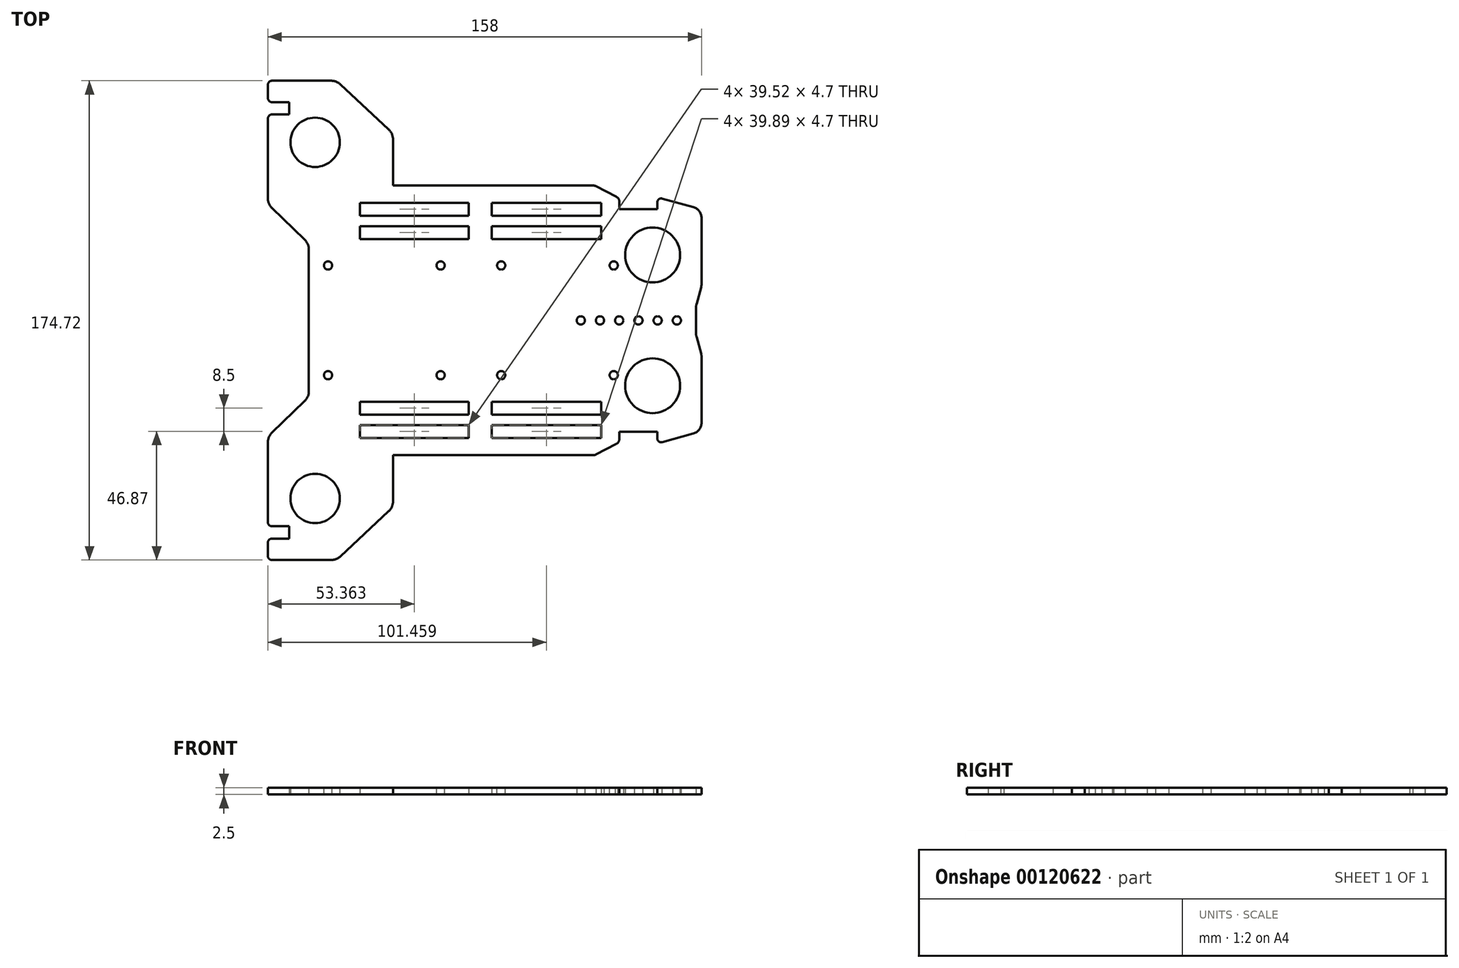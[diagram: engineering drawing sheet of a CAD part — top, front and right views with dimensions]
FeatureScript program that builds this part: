
annotation { "Feature Type Name" : "Feature", "Feature Type Description" : "" }
export const myFeature = defineFeature(function(context is Context, id is Id, definition is map)
    precondition{}
    {
        {
            var Q0;
            Q0=qCreatedBy(makeId("Top.planeOp"),FACE);
            var sketch = newSketch(context, id + "F0", { "sketchPlane" : qUnion([Q0])});
            skLineSegment(sketch, "E0", {"start": v(-81.12, -38.25) * mm, "end": v(74.88, -38.25) * mm});
            skLineSegment(sketch, "E1.bottom", {"start": v(-81.12, -117.81) * mm, "end": v(-73.32, -117.81) * mm});
            skLineSegment(sketch, "E1.top", {"start": v(-81.12, -113.31) * mm, "end": v(-73.32, -113.31) * mm});
            skLineSegment(sketch, "E1.right", {"start": v(-73.32, -117.81) * mm, "end": v(-73.32, -113.31) * mm});
            skLineSegment(sketch, "E2", {"start": v(-66.2, -38.25) * mm, "end": v(-66.2, -66.25) * mm});
            skLineSegment(sketch, "E3", {"start": v(-81.12, -80.61) * mm, "end": v(-66.2, -66.25) * mm});
            skLineSegment(sketch, "E4", {"start": v(-81.12, -80.61) * mm, "end": v(-81.12, -113.31) * mm});
            skLineSegment(sketch, "E5", {"start": v(-81.12, -125.61) * mm, "end": v(-56.12, -125.61) * mm});
            skLineSegment(sketch, "E6", {"start": v(-56.12, -125.61) * mm, "end": v(-35.53, -106.39) * mm});
            skLineSegment(sketch, "E7", {"start": v(-35.53, -106.39) * mm, "end": v(-35.53, -87.39) * mm});
            skLineSegment(sketch, "E8", {"start": v(-35.53, -87.39) * mm, "end": v(38, -87.39) * mm});
            skLineSegment(sketch, "E9", {"start": v(38, -87.39) * mm, "end": v(46.91, -82.75) * mm});
            skLineSegment(sketch, "E10", {"start": v(46.91, -82.75) * mm, "end": v(46.91, -78.85) * mm});
            skLineSegment(sketch, "E11", {"start": v(46.91, -78.85) * mm, "end": v(60.76, -78.85) * mm});
            skLineSegment(sketch, "E12", {"start": v(60.76, -78.85) * mm, "end": v(60.76, -83.16) * mm});
            skLineSegment(sketch, "E13", {"start": v(60.76, -83.16) * mm, "end": v(76.88, -78.68) * mm});
            skLineSegment(sketch, "E14", {"start": v(76.88, -78.68) * mm, "end": v(76.88, -51.04) * mm});
            skLineSegment(sketch, "E15", {"start": v(76.88, -51.04) * mm, "end": v(74.88, -43.67) * mm});
            skLineSegment(sketch, "E16", {"start": v(74.88, -43.67) * mm, "end": v(74.88, -38.25) * mm});
            skLineSegment(sketch, "E17", {"start": v(-81.12, -117.81) * mm, "end": v(-81.12, -125.61) * mm});
            skPoint(sketch, "E18.orphan", {"position": v(76.88, -38.25) * mm});
            skCircle(sketch, "E19", {"center": v(32.88, -38.25) * mm, "radius": 1.5 * mm});
            skCircle(sketch, "E20.1.0.0", {"center": v(39.88, -38.25) * mm, "radius": 1.5 * mm});
            skCircle(sketch, "E20.2.0.0", {"center": v(46.88, -38.25) * mm, "radius": 1.5 * mm});
            skCircle(sketch, "E20.3.0.0", {"center": v(53.88, -38.25) * mm, "radius": 1.5 * mm});
            skCircle(sketch, "E20.4.0.0", {"center": v(60.88, -38.25) * mm, "radius": 1.5 * mm});
            skCircle(sketch, "E20.5.0.0", {"center": v(67.88, -38.25) * mm, "radius": 1.5 * mm});
            skLineSegment(sketch, "E20.direction1", {"start": v(32.88, -38.25) * mm, "end": v(39.88, -38.25) * mm, "construction": true});
            skLineSegment(sketch, "E21.bottom", {"start": v(-47.51, -67.89) * mm, "end": v(-8, -67.89) * mm});
            skLineSegment(sketch, "E21.top", {"start": v(-47.51, -72.59) * mm, "end": v(-8, -72.59) * mm});
            skLineSegment(sketch, "E21.left", {"start": v(-47.51, -67.89) * mm, "end": v(-47.51, -72.59) * mm});
            skLineSegment(sketch, "E21.right", {"start": v(40.28, -67.89) * mm, "end": v(40.28, -72.59) * mm});
            skLineSegment(sketch, "E22.bottom", {"start": v(-47.51, -76.39) * mm, "end": v(-8, -76.39) * mm});
            skLineSegment(sketch, "E22.top", {"start": v(-47.51, -81.09) * mm, "end": v(-8, -81.09) * mm});
            skLineSegment(sketch, "E22.left", {"start": v(-47.51, -76.39) * mm, "end": v(-47.51, -81.09) * mm});
            skLineSegment(sketch, "E22.right", {"start": v(40.28, -76.39) * mm, "end": v(40.28, -81.09) * mm});
            skLineSegment(sketch, "E23", {"start": v(-8, -67.89) * mm, "end": v(-8, -72.59) * mm});
            skLineSegment(sketch, "E24", {"start": v(0.4, -67.89) * mm, "end": v(0.4, -72.59) * mm});
            skLineSegment(sketch, "E25.trimOffspring", {"start": v(0.4, -67.89) * mm, "end": v(40.28, -67.89) * mm});
            skLineSegment(sketch, "E26.trimOffspring", {"start": v(0.4, -72.59) * mm, "end": v(40.28, -72.59) * mm});
            skLineSegment(sketch, "E27.trimOffspring", {"start": v(0.4, -76.39) * mm, "end": v(40.28, -76.39) * mm});
            skLineSegment(sketch, "E28.trimOffspring", {"start": v(0.4, -81.09) * mm, "end": v(40.28, -81.09) * mm});
            skLineSegment(sketch, "E29.trimOffspring", {"start": v(-8, -76.39) * mm, "end": v(-8, -81.09) * mm});
            skLineSegment(sketch, "E30.trimOffspring", {"start": v(0.4, -76.39) * mm, "end": v(0.4, -81.09) * mm});
            skCircle(sketch, "E31", {"center": v(-63.9, -103.18) * mm, "radius": 9 * mm});
            skCircle(sketch, "E32", {"center": v(59.04, -62.08) * mm, "radius": 10 * mm});
            skSolve(sketch);
        }
        {
            var Q0;
            Q0=makeQuery(id+"F0.imprint","IMPRINT",FACE,{"disambiguationData":[TD([[makeQuery(id+"F0.imprint","IMPRINT",EDGE,{"derivedFrom":sQuery(id+"F0.wireOp",EDGE,"E1.bottom")}),-1.0]])]});
            extrude(context, id + "F1", {"entities" : qUnion([Q0]), "depth" : 2.5 * mm});
        }
        {
            var Q0;
            Q0=makeQuery(id+"F1.opExtrude","SWEPT_EDGE",EDGE,{"disambiguationData":[OSD([sQuery(id+"F0.wireOp",EDGE,"E12"),sQuery(id+"F0.wireOp",EDGE,"E13")])]});
            fillet(context, id + "F2", {"entities" : qUnion([Q0]), "radius" : 1.42 * mm, "tangentPropagation" : true, "allowEdgeOverflow" : false});
        }
        {
            var Q0;
            Q0=makeQuery(id+"F1.opExtrude","SWEPT_EDGE",EDGE,{"disambiguationData":[OSD([sQuery(id+"F0.wireOp",EDGE,"E13"),sQuery(id+"F0.wireOp",EDGE,"E14")])]});
            fillet(context, id + "F3", {"entities" : qUnion([Q0]), "radius" : 4.12 * mm, "tangentPropagation" : true, "allowEdgeOverflow" : false});
        }
        {
            var Q0;
            Q0=makeQuery(id+"F1.opExtrude","SWEPT_EDGE",EDGE,{"disambiguationData":[OSD([sQuery(id+"F0.wireOp",EDGE,"E9"),sQuery(id+"F0.wireOp",EDGE,"E10")])]});
            var Q1;
            Q1=makeQuery(id+"F1.opExtrude","SWEPT_EDGE",EDGE,{"disambiguationData":[OSD([sQuery(id+"F0.wireOp",EDGE,"E8"),sQuery(id+"F0.wireOp",EDGE,"E9")])]});
            fillet(context, id + "F4", {"entities" : qUnion([Q0, Q1]), "radius" : 2.06 * mm, "tangentPropagation" : true, "allowEdgeOverflow" : false});
        }
        {
            var Q0;
            Q0=makeQuery(id+"F1.opExtrude","SWEPT_EDGE",EDGE,{"disambiguationData":[OSD([sQuery(id+"F0.wireOp",EDGE,"E5"),sQuery(id+"F0.wireOp",EDGE,"E6")])]});
            var Q1;
            Q1=makeQuery(id+"F1.opExtrude","SWEPT_EDGE",EDGE,{"disambiguationData":[OSD([sQuery(id+"F0.wireOp",EDGE,"E6"),sQuery(id+"F0.wireOp",EDGE,"E7")])]});
            fillet(context, id + "F5", {"entities" : qUnion([Q0, Q1]), "radius" : 5 * mm, "tangentPropagation" : true, "allowEdgeOverflow" : false});
        }
        {
            var Q0;
            Q0=makeQuery(id+"F1.opExtrude","SWEPT_EDGE",EDGE,{"disambiguationData":[OSD([sQuery(id+"F0.wireOp",EDGE,"E1.top"),sQuery(id+"F0.wireOp",EDGE,"E4")])]});
            var Q1;
            Q1=makeQuery(id+"F1.opExtrude","SWEPT_EDGE",EDGE,{"disambiguationData":[OSD([sQuery(id+"F0.wireOp",EDGE,"E1.bottom"),sQuery(id+"F0.wireOp",EDGE,"E17")])]});
            var Q2;
            Q2=makeQuery(id+"F1.opExtrude","SWEPT_EDGE",EDGE,{"disambiguationData":[OSD([sQuery(id+"F0.wireOp",EDGE,"E5"),sQuery(id+"F0.wireOp",EDGE,"E17")])]});
            fillet(context, id + "F6", {"entities" : qUnion([Q0, Q1, Q2]), "radius" : 1.54 * mm, "tangentPropagation" : true, "allowEdgeOverflow" : false});
        }
        {
            var Q0;
            Q0=makeQuery(id+"F1.opExtrude","SWEPT_EDGE",EDGE,{"disambiguationData":[OSD([sQuery(id+"F0.wireOp",EDGE,"E3"),sQuery(id+"F0.wireOp",EDGE,"E4")])]});
            var Q1;
            Q1=makeQuery(id+"F1.opExtrude","SWEPT_EDGE",EDGE,{"disambiguationData":[OSD([sQuery(id+"F0.wireOp",EDGE,"E2"),sQuery(id+"F0.wireOp",EDGE,"E3")])]});
            fillet(context, id + "F7", {"entities" : qUnion([Q0, Q1]), "radius" : 5 * mm, "tangentPropagation" : true, "allowEdgeOverflow" : false});
        }
        {
            var Q0;
            Q0=makeQuery(id+"F1.opExtrude","SWEPT_EDGE",EDGE,{"disambiguationData":[OSD([sQuery(id+"F0.wireOp",EDGE,"E14"),sQuery(id+"F0.wireOp",EDGE,"E15")])]});
            var Q1;
            Q1=makeQuery(id+"F1.opExtrude","SWEPT_EDGE",EDGE,{"disambiguationData":[OSD([sQuery(id+"F0.wireOp",EDGE,"E15"),sQuery(id+"F0.wireOp",EDGE,"E16")])]});
            fillet(context, id + "F8", {"entities" : qUnion([Q0, Q1]), "radius" : 5 * mm, "tangentPropagation" : true, "allowEdgeOverflow" : false});
        }
        {
            var Q0;
            Q0=makeQuery(id+"F1.opExtrude","SWEPT_BODY",BODY,{"disambiguationData":[OSD([sQuery(id+"F0.wireOp",EDGE,"E0"),sQuery(id+"F0.wireOp",EDGE,"E1.bottom"),sQuery(id+"F0.wireOp",EDGE,"E1.top"),sQuery(id+"F0.wireOp",EDGE,"E1.right"),sQuery(id+"F0.wireOp",EDGE,"E2"),sQuery(id+"F0.wireOp",EDGE,"E3"),sQuery(id+"F0.wireOp",EDGE,"E4"),sQuery(id+"F0.wireOp",EDGE,"E5"),sQuery(id+"F0.wireOp",EDGE,"E6"),sQuery(id+"F0.wireOp",EDGE,"E7"),sQuery(id+"F0.wireOp",EDGE,"E8"),sQuery(id+"F0.wireOp",EDGE,"E9"),sQuery(id+"F0.wireOp",EDGE,"E10"),sQuery(id+"F0.wireOp",EDGE,"E11"),sQuery(id+"F0.wireOp",EDGE,"E12"),sQuery(id+"F0.wireOp",EDGE,"E13"),sQuery(id+"F0.wireOp",EDGE,"E14"),sQuery(id+"F0.wireOp",EDGE,"E15"),sQuery(id+"F0.wireOp",EDGE,"E16"),sQuery(id+"F0.wireOp",EDGE,"E17"),sQuery(id+"F0.wireOp",EDGE,"E19"),sQuery(id+"F0.wireOp",EDGE,"E20.1.0.0"),sQuery(id+"F0.wireOp",EDGE,"E20.2.0.0"),sQuery(id+"F0.wireOp",EDGE,"E20.3.0.0"),sQuery(id+"F0.wireOp",EDGE,"E20.4.0.0"),sQuery(id+"F0.wireOp",EDGE,"E20.5.0.0"),sQuery(id+"F0.wireOp",EDGE,"E21.bottom"),sQuery(id+"F0.wireOp",EDGE,"E21.top"),sQuery(id+"F0.wireOp",EDGE,"E21.left"),sQuery(id+"F0.wireOp",EDGE,"E21.right"),sQuery(id+"F0.wireOp",EDGE,"E22.bottom"),sQuery(id+"F0.wireOp",EDGE,"E22.top"),sQuery(id+"F0.wireOp",EDGE,"E22.left"),sQuery(id+"F0.wireOp",EDGE,"E22.right"),sQuery(id+"F0.wireOp",EDGE,"E23"),sQuery(id+"F0.wireOp",EDGE,"E24"),sQuery(id+"F0.wireOp",EDGE,"E25.trimOffspring"),sQuery(id+"F0.wireOp",EDGE,"E26.trimOffspring"),sQuery(id+"F0.wireOp",EDGE,"E27.trimOffspring"),sQuery(id+"F0.wireOp",EDGE,"E28.trimOffspring"),sQuery(id+"F0.wireOp",EDGE,"E29.trimOffspring"),sQuery(id+"F0.wireOp",EDGE,"E30.trimOffspring"),sQuery(id+"F0.wireOp",EDGE,"E31"),sQuery(id+"F0.wireOp",EDGE,"E32")])]});
            var Q1;
            {var subQ0=sQuery(id+"F0.wireOp",EDGE,"E0");Q1=makeQuery(id+"F1.opExtrude","SWEPT_FACE",FACE,{"disambiguationData":[OSD([subQ0]),TDD([makeQuery(id+"F0.imprint","IMPRINT",EDGE,{"disambiguationData":[TD([[makeQuery(id+"F0.imprint","INTERSECT",VERTEX,{"derivedFrom":[subQ0,sQuery(id+"F0.wireOp",EDGE,"E2")]}),-1.0]])],"derivedFrom":subQ0})])]});}
            mirror(context, id + "F9", {"operationType" : NewBodyOperationType.ADD, "entities" : qUnion([Q0]), "mirrorPlane" : qUnion([Q1])});
        }
        {
            var Q0;
            {var subQ0=makeQuery(id+"F1.opExtrude","CAP_FACE",FACE,{"disambiguationData":[OSD([sQuery(id+"F0.wireOp",EDGE,"E0"),sQuery(id+"F0.wireOp",EDGE,"E1.bottom"),sQuery(id+"F0.wireOp",EDGE,"E1.top"),sQuery(id+"F0.wireOp",EDGE,"E1.right"),sQuery(id+"F0.wireOp",EDGE,"E2"),sQuery(id+"F0.wireOp",EDGE,"E3"),sQuery(id+"F0.wireOp",EDGE,"E4"),sQuery(id+"F0.wireOp",EDGE,"E5"),sQuery(id+"F0.wireOp",EDGE,"E6"),sQuery(id+"F0.wireOp",EDGE,"E7"),sQuery(id+"F0.wireOp",EDGE,"E8"),sQuery(id+"F0.wireOp",EDGE,"E9"),sQuery(id+"F0.wireOp",EDGE,"E10"),sQuery(id+"F0.wireOp",EDGE,"E11"),sQuery(id+"F0.wireOp",EDGE,"E12"),sQuery(id+"F0.wireOp",EDGE,"E13"),sQuery(id+"F0.wireOp",EDGE,"E14"),sQuery(id+"F0.wireOp",EDGE,"E15"),sQuery(id+"F0.wireOp",EDGE,"E16"),sQuery(id+"F0.wireOp",EDGE,"E17"),sQuery(id+"F0.wireOp",EDGE,"E19"),sQuery(id+"F0.wireOp",EDGE,"E20.1.0.0"),sQuery(id+"F0.wireOp",EDGE,"E20.2.0.0"),sQuery(id+"F0.wireOp",EDGE,"E20.3.0.0"),sQuery(id+"F0.wireOp",EDGE,"E20.4.0.0"),sQuery(id+"F0.wireOp",EDGE,"E20.5.0.0"),sQuery(id+"F0.wireOp",EDGE,"E21.bottom"),sQuery(id+"F0.wireOp",EDGE,"E21.top"),sQuery(id+"F0.wireOp",EDGE,"E21.left"),sQuery(id+"F0.wireOp",EDGE,"E21.right"),sQuery(id+"F0.wireOp",EDGE,"E22.bottom"),sQuery(id+"F0.wireOp",EDGE,"E22.top"),sQuery(id+"F0.wireOp",EDGE,"E22.left"),sQuery(id+"F0.wireOp",EDGE,"E22.right"),sQuery(id+"F0.wireOp",EDGE,"E23"),sQuery(id+"F0.wireOp",EDGE,"E24"),sQuery(id+"F0.wireOp",EDGE,"E25.trimOffspring"),sQuery(id+"F0.wireOp",EDGE,"E26.trimOffspring"),sQuery(id+"F0.wireOp",EDGE,"E27.trimOffspring"),sQuery(id+"F0.wireOp",EDGE,"E28.trimOffspring"),sQuery(id+"F0.wireOp",EDGE,"E29.trimOffspring"),sQuery(id+"F0.wireOp",EDGE,"E30.trimOffspring"),sQuery(id+"F0.wireOp",EDGE,"E31"),sQuery(id+"F0.wireOp",EDGE,"E32")])],"isStart":false});Q0=makeQuery(id+"F9.boolean.opBoolean","MERGE",FACE,{"derivedFrom":[subQ0,makeQuery(id+"F9.opPattern","COPY",FACE,{"derivedFrom":subQ0,"instanceName":"1"})]});}
            var sketch = newSketch(context, id + "F10", { "sketchPlane" : qUnion([Q0])});
            skLineSegment(sketch, "E33", {"start": v(-66.2, -38.25) * mm, "end": v(74.88, -38.25) * mm, "construction": true});
            skLineSegment(sketch, "E34.bottom", {"start": v(-18.2, -18.25) * mm, "end": v(-59.2, -18.25) * mm, "construction": true});
            skLineSegment(sketch, "E34.top", {"start": v(-18.2, -58.25) * mm, "end": v(-59.2, -58.25) * mm, "construction": true});
            skLineSegment(sketch, "E34.left", {"start": v(-18.2, -18.25) * mm, "end": v(-18.2, -58.25) * mm, "construction": true});
            skLineSegment(sketch, "E34.right", {"start": v(-59.2, -18.25) * mm, "end": v(-59.2, -58.25) * mm, "construction": true});
            skPoint(sketch, "E34.middle", {"position": v(-38.7, -38.25) * mm});
            skCircle(sketch, "E35", {"center": v(-59.2, -18.25) * mm, "radius": 1.5 * mm});
            skCircle(sketch, "E36", {"center": v(-18.2, -18.25) * mm, "radius": 1.5 * mm});
            skCircle(sketch, "E37", {"center": v(-18.2, -58.25) * mm, "radius": 1.5 * mm});
            skCircle(sketch, "E38", {"center": v(-59.2, -58.25) * mm, "radius": 1.5 * mm});
            skLineSegment(sketch, "E39.bottom", {"start": v(3.88, -18.25) * mm, "end": v(44.88, -18.25) * mm, "construction": true});
            skLineSegment(sketch, "E39.top", {"start": v(3.88, -58.25) * mm, "end": v(44.88, -58.25) * mm, "construction": true});
            skLineSegment(sketch, "E39.left", {"start": v(3.88, -18.25) * mm, "end": v(3.88, -58.25) * mm, "construction": true});
            skLineSegment(sketch, "E39.right", {"start": v(44.88, -18.25) * mm, "end": v(44.88, -58.25) * mm, "construction": true});
            skPoint(sketch, "E39.middle", {"position": v(24.38, -38.25) * mm});
            skCircle(sketch, "E40", {"center": v(3.88, -18.25) * mm, "radius": 1.5 * mm});
            skCircle(sketch, "E41", {"center": v(44.88, -18.25) * mm, "radius": 1.5 * mm});
            skCircle(sketch, "E42", {"center": v(3.88, -58.25) * mm, "radius": 1.5 * mm});
            skCircle(sketch, "E43", {"center": v(44.88, -58.25) * mm, "radius": 1.5 * mm});
            skSolve(sketch);
        }
        {
            var Q0;
            Q0=makeQuery(id+"F10.imprint","IMPRINT",FACE,{"disambiguationData":[TD([[makeQuery(id+"F10.imprint","IMPRINT",EDGE,{"derivedFrom":sQuery(id+"F10.wireOp",EDGE,"E35")}),1.0]])]});
            var Q1;
            Q1=makeQuery(id+"F10.imprint","IMPRINT",FACE,{"disambiguationData":[TD([[makeQuery(id+"F10.imprint","IMPRINT",EDGE,{"derivedFrom":sQuery(id+"F10.wireOp",EDGE,"E36")}),1.0]])]});
            var Q2;
            Q2=makeQuery(id+"F10.imprint","IMPRINT",FACE,{"disambiguationData":[TD([[makeQuery(id+"F10.imprint","IMPRINT",EDGE,{"derivedFrom":sQuery(id+"F10.wireOp",EDGE,"E37")}),1.0]])]});
            var Q3;
            Q3=makeQuery(id+"F10.imprint","IMPRINT",FACE,{"disambiguationData":[TD([[makeQuery(id+"F10.imprint","IMPRINT",EDGE,{"derivedFrom":sQuery(id+"F10.wireOp",EDGE,"E38")}),1.0]])]});
            var Q4;
            Q4=makeQuery(id+"F10.imprint","IMPRINT",FACE,{"disambiguationData":[TD([[makeQuery(id+"F10.imprint","IMPRINT",EDGE,{"derivedFrom":sQuery(id+"F10.wireOp",EDGE,"E40")}),1.0]])]});
            var Q5;
            Q5=makeQuery(id+"F10.imprint","IMPRINT",FACE,{"disambiguationData":[TD([[makeQuery(id+"F10.imprint","IMPRINT",EDGE,{"derivedFrom":sQuery(id+"F10.wireOp",EDGE,"E42")}),1.0]])]});
            var Q6;
            Q6=makeQuery(id+"F10.imprint","IMPRINT",FACE,{"disambiguationData":[TD([[makeQuery(id+"F10.imprint","IMPRINT",EDGE,{"derivedFrom":sQuery(id+"F10.wireOp",EDGE,"E43")}),1.0]])]});
            var Q7;
            Q7=makeQuery(id+"F10.imprint","IMPRINT",FACE,{"disambiguationData":[TD([[makeQuery(id+"F10.imprint","IMPRINT",EDGE,{"derivedFrom":sQuery(id+"F10.wireOp",EDGE,"E41")}),1.0]])]});
            var Q8;
            Q8=sQuery(id+"F10.wireOp",EDGE,"E35");
            extrude(context, id + "F11", {"entities" : qUnion([Q0, Q1, Q2, Q3, Q4, Q5, Q6, Q7]), "operationType" : NewBodyOperationType.REMOVE, "surfaceEntities" : qUnion([Q8]), "oppositeDirection" : true, "depth" : 25 * mm});
        }
    });
